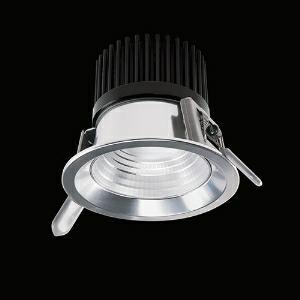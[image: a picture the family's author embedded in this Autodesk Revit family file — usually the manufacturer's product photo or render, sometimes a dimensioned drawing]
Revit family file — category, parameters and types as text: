
# Revit family: spectral_myral_myral_4500-840-s-dali
name_source: partatom
category: Lighting Fixtures
revit_build: Autodesk Revit 2016 (Build: 20150220_1215(x64)
units: mm (PartAtom-declared; Revit-internal decimal feet)

## family parameters
Cut with Voids When Loaded = No
Host = Face
Light Source = No
Part Type = Normal
Room Calculation Point = No
Round Connector Dimension = Use Diameter
Shared = No

## types (1)
- SPECTRAL MYRAL (1 x )
    Apparent Load = 0 VA
    Approval mark = CE
    CIE Flux Codes = 85 100 100 100 100
    Control Gear = Electronic transformer
    Default Elevation = 1800 mm
    Description = SPG0330177
MYRAL recessed spot

Design:
    Height = 0 mm  [stored 0 ft]
    Lamp = 1 x
    Lamp count = 1
    Length = 120 mm
    Luminous efficacy = 0 lm/W
    Manufacturer = Ridi
    ModVariant = No
    Model = MYRAL 4500-840-S-DALI
    Mounting Place = Ceiling
    Mounting Type = Recessed
    Number of Poles = 1
    OnlyDefault = Yes
    Power Factor = 1
    Product Name = SPECTRAL MYRAL
    Product group = Downlight recessed
    ProductGroupID = 400
    Protection Class = Protection class
    Protection Degree = IP 20
    RlxData = <blob elided: 38937 chars, md5=af8408e6>
    Socket = socket
    Standby Power = 0 W
    System Light Flux = 0 lm
    System Power = 0 W
    Type Image = myral_04.jpg
    URL = http://reluxnet.relux.com
    VarID = ---
    Voltage = 0 V
    Weight = 0.00 kg
    Width = 0 mm  [stored 0 ft]

note: [stored X ft] marks values corroborated as IEEE doubles in the binary element streams (Revit-internal decimal feet)

## geometry (parser evidence)
native form markers: Sweep x9
no freeform markers — native parametric forms only
